# Revit family: 82QET_231217_1
name_source: partatom
category: 통신 장치
units: mm (PartAtom-declared; Revit-internal decimal feet)

## family parameters
OmniClass 번호 = 23.85.10.14.24
OmniClass 제목 = Video Monitors
공유 = 아니오
로드될 때 보이드를 사용하여 절단 = 아니오
룸 계산 점 = 아니오
부품 유형 = 보통
원형 커넥터 치수 = 지름 사용
작업 기준면 기반 = 아니오
주석 방향을 유지합니다. = 아니오
항상 수직 = 예

## types (1)
- UHD Signage QE82T
    Active Display Area = 1805.76(H) x 1015.74(V)
    Bezel Width = 3 Bezel-less
    Brightness (Typ.) = 300
    Color Gamut = (NTSC) 72%
    Contrast Ratio (Typ.) = 4000:1
    Diagonal Size (Class) = 82  [stored 0.269029 ft]
    Diagonal Size (Measured) = 81.5
    Dimension Package (mm) = 2033 x 1209 x 290
    Dimension Set (mm) = 1829.9 x 1045 x 59.9
    Dimension Set Depth (mm) = 59.9
    Dimension Set Height (mm) = 1045  [stored 3.42848 ft]
    Dimension Set Width (mm) = 1829.9  [stored 6.00361 ft]
    Display Colors = 16.7M(True Display)
    Dynamic C/R = MEGA
    EMC = Class B
    External Control = RS232C(in/out) thru stereo jack, RJ45
    H-Scanning Frequency = 30 ~ 81kHZ
    Haze = 2%
    Input HDCP = HDCP2.2
    Input RGB = -
    Input USB = USB 2.0 x 1
    Input Video = HDMI 2.0 (2)
    Internal Clock Speed = 1.7GHz
    Internal Graphics = Graphic resolution : 1920x1080, Output resolution : 3840x2160 (Scale up from graphic processing result.)
    Internal IO Ports = USB 2.0
    Internal Main Memory Interface = 2.0GB, LPDDR4 1.5GHz 64bit
    Internal Multimedia = Video Decoder  : MPEG-1/2/4, H.263, H.264/AVC, UHD H.264/AVC,  VC-1, AVS+, HEVC, JPEG, PNG, VP8, VP9  *Audio Decoder : AC3 (DD), MPEG
    Internal On-Chip Cache Memory = L1 Instruction Cache : 48KB L1 Data Cache : 32KB L2 Cache : 2MB
    Internal Operating System = Tizen 4.0 (VDLinux)
    Internal Processor = Cortex A72 1.7GHz Quad-Core CPU
    Internal Storage (FDM) = 8GB (3.88GB Occupied by O/S, 4.12GB Available)
    Key = UHD Signage with Built-in MagicInfo Lite
    Maximum Pixel Frequency = 594MHz
    Operation Hour = 16/7
    Optional Mount = WMN8200SF / WMN8200SG (Land Only)
    Orientation = Landscape
    Output Audio = Stereo mini Jack
    Pixel Pitch (mm) = 0.47025 x 0.47025
    Power Consumption BTU(Max) = 937.8
    Power Consumption Max [W/h] = 275
    Power Consumption Rating [W/h] = 250
    Power Consumption Sleep mode = 0.5
    Power Consumption Typical [W/h] = 211
    Power Supply = AC 100 - 240 V, 50/60 Hz
    Power Type = Internal
    Relative Humidity = 10~80%
    Resolution = UHD (3840 x 2160)
    Response Time (GtoG) = 8ms
    Safety = 60950-1
    Screen = Samsung Electronics Screen
    Security = -
    Sound = Built in Speaker(10W + 10W)
    Stand Type = No
    Temperature = 0℃ ~ 40℃
    Type = Direct LED BLU
    V-Scanning Frequency = 48 ~ 75HZ
    VESA Mount = 600 X 400
    Viewing Angle(H/V) = 178/178
    Weight Package (kg) = 52.1
    Weight Set (kg) = 37.5
    모델 = UHD Signage QE82T
    제조업체 = Samsung Electronics Co., Ltd.
    조합 코드 = E1020500
    키노트 = 11 52 00

note: [stored X ft] marks values corroborated as IEEE doubles in the binary element streams (Revit-internal decimal feet)
